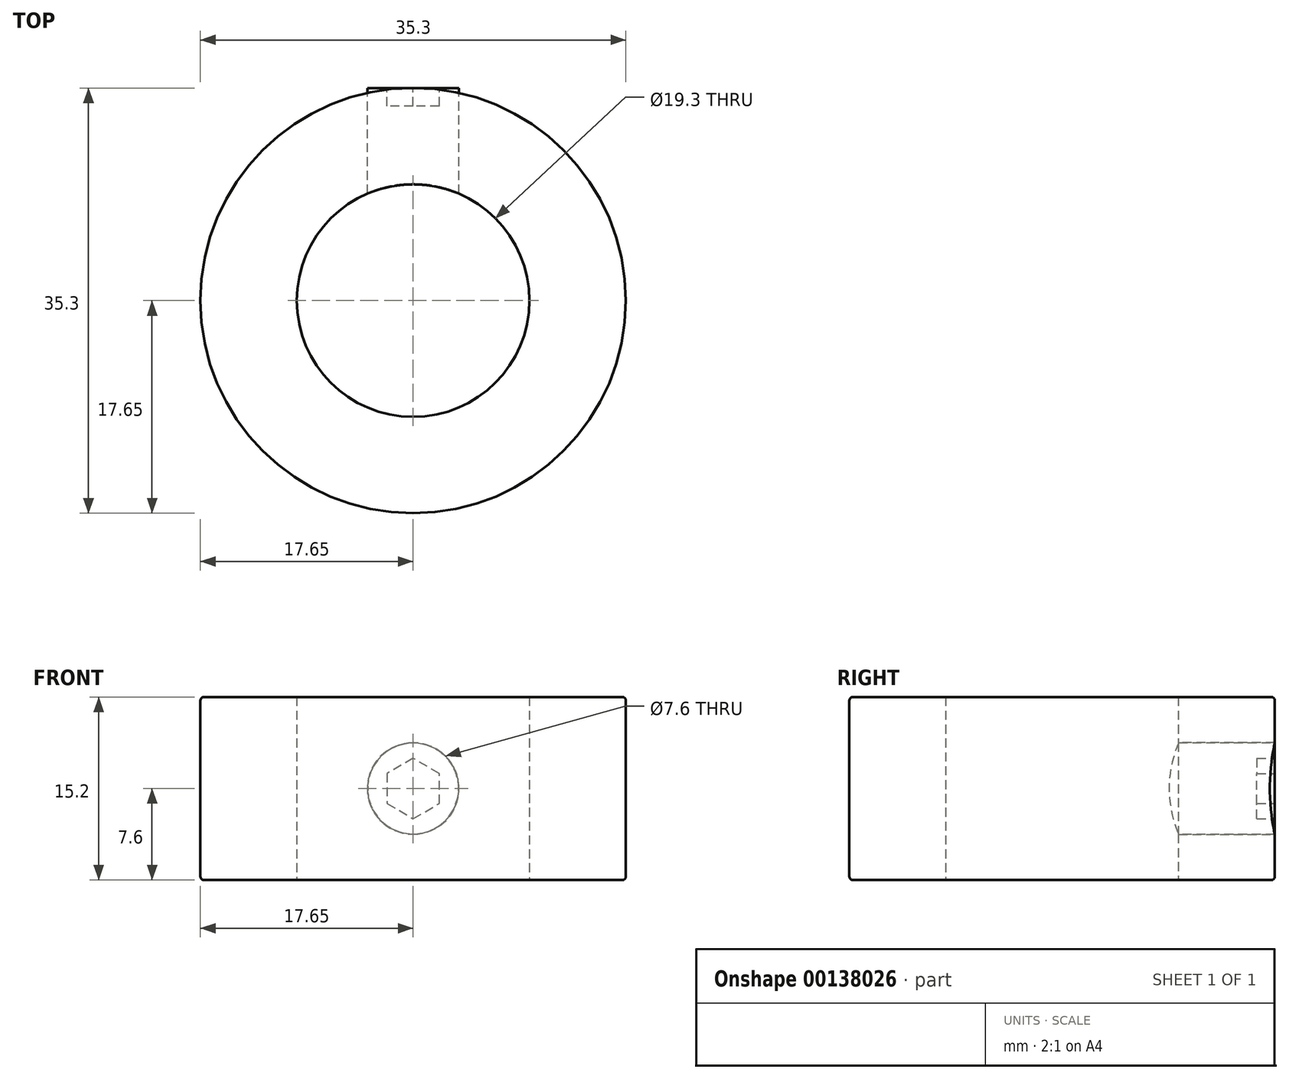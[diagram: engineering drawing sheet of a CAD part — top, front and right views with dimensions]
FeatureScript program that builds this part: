
annotation { "Feature Type Name" : "Feature", "Feature Type Description" : "" }
export const myFeature = defineFeature(function(context is Context, id is Id, definition is map)
    precondition{}
    {
        {
            var Q0;
            Q0=qCreatedBy(makeId("Top.planeOp"),FACE);
            var sketch = newSketch(context, id + "F0", { "sketchPlane" : qUnion([Q0])});
            skCircle(sketch, "E0", {"center": v(0, 0) * mm, "radius": 9.65 * mm});
            skCircle(sketch, "E1", {"center": v(0, 0) * mm, "radius": 17.65 * mm});
            skSolve(sketch);
        }
        {
            var Q0;
            Q0=qSketchRegion(id+"F0",true);
            extrude(context, id + "F1", {"entities" : qUnion([Q0]), "depth" : 15.2 * mm});
        }
        {
            var Q0;
            Q0=makeQuery(id+"F1.opExtrude","CAP_EDGE",EDGE,{"disambiguationData":[OSD([sQuery(id+"F0.wireOp",EDGE,"E1")])],"isStart":false});
            var Q1;
            Q1=makeQuery(id+"F1.opExtrude","SWEPT_FACE",FACE,{"disambiguationData":[OSD([sQuery(id+"F0.wireOp",EDGE,"E1")])]});
            fillet(context, id + "F2", {"entities" : qUnion([Q0, Q1]), "radius" : 0.3 * mm, "tangentPropagation" : true, "allowEdgeOverflow" : false});
        }
        {
            var Q0;
            Q0=qCreatedBy(makeId("Front.planeOp"),FACE);
            var sketch = newSketch(context, id + "F3", { "sketchPlane" : qUnion([Q0])});
            skCircle(sketch, "E2", {"center": v(0, 7.6) * mm, "radius": 3.8 * mm});
            skSolve(sketch);
        }
        {
            var Q0;
            Q0 = qSketchRegion(id + "F3", true);
            extrude(context, id + "F4", {"entities" : qUnion([Q0]), "operationType" : NewBodyOperationType.REMOVE, "endBound" : BoundingType.THROUGH_ALL, "oppositeDirection" : true, "depth" : 25 * mm});
        }
        {
            var Q0;
            Q0=qCreatedBy(makeId("Front.planeOp"),FACE);
            cPlane(context, id + "F5", {"entities" : qUnion([Q0]), "cplaneType" : CPlaneType.OFFSET, "offset" : (35.3 / 2) * mm, "oppositeDirection" : true, "width" : 150 * mm, "height" : 150 * mm});
        }
        {
            var Q0;
            Q0=qCreatedBy(id+"F5.planeOp",FACE);
            var sketch = newSketch(context, id + "F6", { "sketchPlane" : qUnion([Q0])});
            skCircle(sketch, "E3.0", {"center": v(0, 7.6) * mm, "radius": 3.8 * mm});
            skSolve(sketch);
        }
        {
            var Q0;
            Q0 = qSketchRegion(id + "F6", true);
            var Q1;
            Q1=makeQuery(id+"F1.opExtrude","SWEPT_FACE",FACE,{"disambiguationData":[OSD([sQuery(id+"F0.wireOp",EDGE,"E0")])]});
            extrude(context, id + "F7", {"entities" : qUnion([Q0]), "endBound" : BoundingType.UP_TO_SURFACE, "endBoundEntityFace" : qUnion([Q1]), "depth" : 25 * mm});
        }
        {
            var Q0;
            Q0=makeQuery(id+"F7.opExtrude","CAP_FACE",FACE,{"disambiguationData":[OSD([sQuery(id+"F6.wireOp",EDGE,"E3.0")])],"isStart":true});
            var sketch = newSketch(context, id + "F8", { "sketchPlane" : qUnion([Q0])});
            skCircle(sketch, "E4.cCircle", {"center": v(0, 7.6) * mm, "radius": 2.5 * mm, "construction": true});
            skLineSegment(sketch, "E4.0", {"start": v(0, 10.1) * mm, "end": v(2.17, 8.85) * mm});
            skLineSegment(sketch, "E4.1", {"start": v(2.17, 8.85) * mm, "end": v(2.17, 6.35) * mm});
            skLineSegment(sketch, "E4.2", {"start": v(2.17, 6.35) * mm, "end": v(0, 5.1) * mm});
            skLineSegment(sketch, "E4.3", {"start": v(0, 5.1) * mm, "end": v(-2.17, 6.35) * mm});
            skLineSegment(sketch, "E4.4", {"start": v(-2.17, 6.35) * mm, "end": v(-2.17, 8.85) * mm});
            skLineSegment(sketch, "E4.5", {"start": v(-2.17, 8.85) * mm, "end": v(0, 10.1) * mm});
            skSolve(sketch);
        }
        {
            var Q0;
            Q0=makeQuery(id+"F8.imprint","IMPRINT",FACE,{"disambiguationData":[TD([[makeQuery(id+"F8.imprint","IMPRINT",EDGE,{"derivedFrom":sQuery(id+"F8.wireOp",EDGE,"E4.0")}),-1.0]])]});
            extrude(context, id + "F9", {"entities" : qUnion([Q0]), "operationType" : NewBodyOperationType.REMOVE, "oppositeDirection" : true, "depth" : 1.5 * mm});
        }
    });
